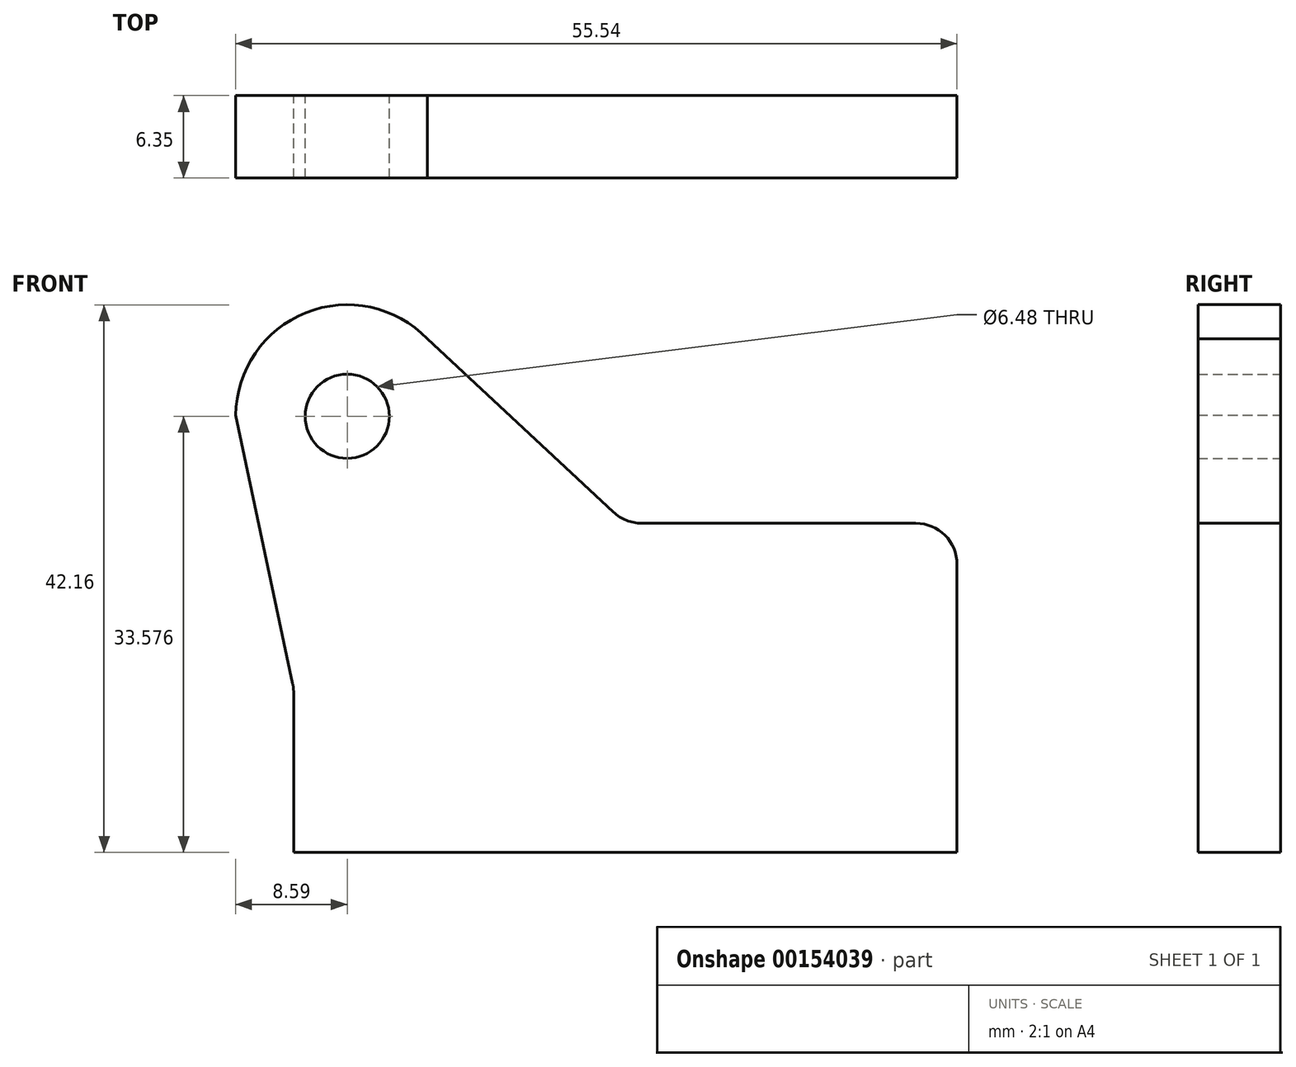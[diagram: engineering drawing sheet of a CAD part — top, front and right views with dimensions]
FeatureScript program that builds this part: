
annotation { "Feature Type Name" : "Feature", "Feature Type Description" : "" }
export const myFeature = defineFeature(function(context is Context, id is Id, definition is map)
    precondition{}
    {
        {
            var Q0;
            Q0=qCreatedBy(makeId("Front.planeOp"),FACE);
            var sketch = newSketch(context, id + "F0", { "sketchPlane" : qUnion([Q0])});
            skLineSegment(sketch, "E0.bottom", {"start": v(-2.1, 18.22) * mm, "end": v(19.02, 18.22) * mm});
            skLineSegment(sketch, "E0.top", {"start": v(-28.89, -7.13) * mm, "end": v(22.2, -7.13) * mm});
            skLineSegment(sketch, "E0.left", {"start": v(-28.89, 5.2) * mm, "end": v(-28.89, -7.13) * mm});
            skLineSegment(sketch, "E0.right", {"start": v(22.2, 15.04) * mm, "end": v(22.2, -7.13) * mm});
            skCircle(sketch, "E1", {"center": v(-24.76, 26.45) * mm, "radius": 3.24 * mm});
            skArc(sketch, "E2", {"start": v(-18.59, 32.41) * mm, "mid": v(-27.94, 34.42) * mm, "end": v(-33.35, 26.53) * mm});
            skLineSegment(sketch, "E3", {"start": v(-33.35, 26.53) * mm, "end": v(-28.96, 5.87) * mm});
            skLineSegment(sketch, "E4", {"start": v(-19.25, 33.03) * mm, "end": v(-4.26, 19.07) * mm});
            skPoint(sketch, "E5.orphan", {"position": v(-28.89, 18.22) * mm});
            skPoint(sketch, "E6.visualSharp", {"position": v(22.2, 18.22) * mm});
            skArc(sketch, "E6.filletArc", {"start": v(22.2, 15.04) * mm, "mid": v(21.26, 17.29) * mm, "end": v(19.02, 18.22) * mm});
            skPoint(sketch, "E7.visualSharp", {"position": v(-3.35, 18.22) * mm});
            skArc(sketch, "E7.filletArc", {"start": v(-4.26, 19.07) * mm, "mid": v(-3.26, 18.44) * mm, "end": v(-2.1, 18.22) * mm});
            skPoint(sketch, "E8.visualSharp", {"position": v(-28.89, 5.54) * mm});
            skArc(sketch, "E8.filletArc", {"start": v(-28.89, 5.2) * mm, "mid": v(-28.9, 5.54) * mm, "end": v(-28.96, 5.87) * mm});
            skSolve(sketch);
        }
        {
            var Q0;
            Q0 = qSketchRegion(id + "F0", true);
            extrude(context, id + "F1", {"entities" : qUnion([Q0]), "depth" : 6.35 * mm});
        }
    });
